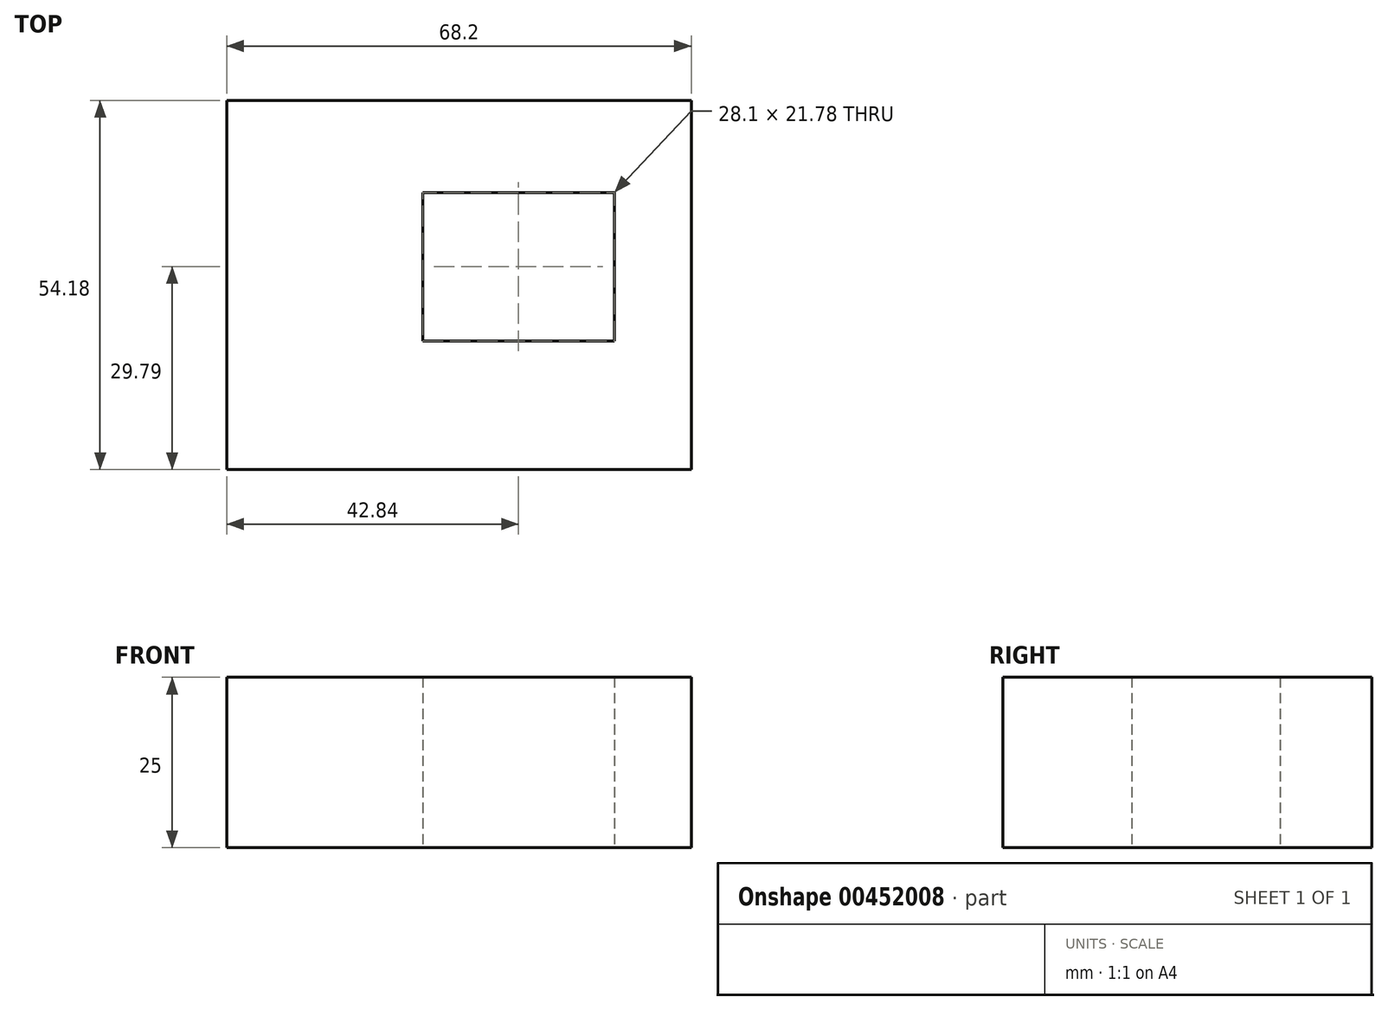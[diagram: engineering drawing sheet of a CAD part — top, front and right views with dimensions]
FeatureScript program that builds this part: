
annotation { "Feature Type Name" : "Feature", "Feature Type Description" : "" }
export const myFeature = defineFeature(function(context is Context, id is Id, definition is map)
    precondition{}
    {
        {
            var Q0;
            Q0=qCreatedBy(makeId("Top.planeOp"),FACE);
            var sketch = newSketch(context, id + "F0", { "sketchPlane" : qUnion([Q0])});
            skLineSegment(sketch, "E0.bottom", {"start": v(-28.79, 30.4) * mm, "end": v(39.41, 30.4) * mm});
            skLineSegment(sketch, "E0.top", {"start": v(-28.79, -23.77) * mm, "end": v(39.41, -23.77) * mm});
            skLineSegment(sketch, "E0.left", {"start": v(-28.79, 30.4) * mm, "end": v(-28.79, -23.77) * mm});
            skLineSegment(sketch, "E0.right", {"start": v(39.41, 30.4) * mm, "end": v(39.41, -23.77) * mm});
            skSolve(sketch);
        }
        {
            var Q0;
            Q0=makeQuery(id+"F0.imprint","IMPRINT",FACE,{"disambiguationData":[TD([[makeQuery(id+"F0.imprint","IMPRINT",EDGE,{"derivedFrom":sQuery(id+"F0.wireOp",EDGE,"E0.bottom")}),-1.0]])]});
            var Q1;
            Q1=sQuery(id+"F0.wireOp",EDGE,"E0.right");
            extrude(context, id + "F1", {"entities" : qUnion([Q0]), "surfaceEntities" : qUnion([Q1]), "depth" : 25 * mm});
        }
        {
            var Q0;
            Q0=makeQuery(id+"F1.opExtrude","CAP_FACE",FACE,{"disambiguationData":[OSD([sQuery(id+"F0.wireOp",EDGE,"E0.bottom"),sQuery(id+"F0.wireOp",EDGE,"E0.top"),sQuery(id+"F0.wireOp",EDGE,"E0.left"),sQuery(id+"F0.wireOp",EDGE,"E0.right")])],"isStart":true});
            var sketch = newSketch(context, id + "F2", { "sketchPlane" : qUnion([Q0])});
            skLineSegment(sketch, "E1.bottom", {"start": v(0, 4.87) * mm, "end": v(28.1, 4.87) * mm});
            skLineSegment(sketch, "E1.top", {"start": v(0, -16.9) * mm, "end": v(28.1, -16.9) * mm});
            skLineSegment(sketch, "E1.left", {"start": v(0, 4.87) * mm, "end": v(0, -16.9) * mm});
            skLineSegment(sketch, "E1.right", {"start": v(28.1, 4.87) * mm, "end": v(28.1, -16.9) * mm});
            skSolve(sketch);
        }
        {
            var Q0;
            Q0=makeQuery(id+"F2.imprint","IMPRINT",FACE,{"disambiguationData":[TD([[makeQuery(id+"F2.imprint","IMPRINT",EDGE,{"derivedFrom":sQuery(id+"F2.wireOp",EDGE,"E1.bottom")}),-1.0]])]});
            extrude(context, id + "F3", {"entities" : qUnion([Q0]), "operationType" : NewBodyOperationType.REMOVE, "oppositeDirection" : true, "depth" : 25 * mm});
        }
    });
